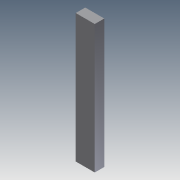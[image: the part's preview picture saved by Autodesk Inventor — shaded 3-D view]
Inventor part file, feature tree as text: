
AUTODESK INVENTOR PART (.ipt)
format: ipt  version: 2011 (Build 150239000, 239)  size: 665,088 bytes
history: native  units: in
note: dims shown in document units (in); Inventor stores cm internally (conversion verified against a paired STEP export)
features: extrude x32, sketch x32
ambient origin geometry x8: Origin, YZ Plane, XZ Plane, XY Plane, X Axis, Y Axis, Z Axis, Center Point
bodies: Solid1 (feature_tree)
feature tree (64):
  extrude  "Extrusion1"  Depth=6.75in
  extrude  "Extrusion2"  Depth=0.5in
  extrude  "Extrusion3"  Depth=0.5in
  extrude  "Extrusion4"  Depth=5.75in
  extrude  "Extrusion5"  Depth=0.5in
  extrude  "Extrusion6"  Depth=1.5in
  extrude  "Extrusion7"  Depth=1.5in
  extrude  "Extrusion8"  Depth=0.156in
  extrude  "Extrusion9"  Depth=0.25in TaperAngle=0.0deg
  extrude  "Extrusion10"  Depth=0.25in TaperAngle=0.0deg
  extrude  "Extrusion11"  Depth=0.25in TaperAngle=0.0deg
  extrude  "Extrusion12"  Depth=0.25in
  extrude  "Extrusion13"  Depth=0.25in
  extrude  "Extrusion14"  Depth=0.25in TaperAngle=0.0deg
  extrude  "Extrusion15"  Depth=3.0in
  extrude  "Extrusion16"  Depth=0.25in TaperAngle=0.0deg
  extrude  "Extrusion17"  Depth=1.0in
  extrude  "Extrusion18"  Depth=0.25in TaperAngle=0.0deg
  extrude  "Extrusion19"  Depth=0.25in TaperAngle=0.0deg
  extrude  "Extrusion20"  Depth=0.25in TaperAngle=0.0deg
  extrude  "Extrusion21"  Depth=1.0in
  extrude  "Extrusion22"  Depth=1.0in
  extrude  "Extrusion23"  Depth=2.0in
  extrude  "Extrusion24"  Depth=0.5in
  extrude  "Extrusion25"  Depth=0.5in
  extrude  "Extrusion26"  Depth=0.5in
  extrude  "Extrusion27"  Depth=0.5in
  extrude  "Extrusion28"  Depth=0.5in
  extrude  "Extrusion29"  Depth=0.5in
  extrude  "Extrusion30"  Depth=0.25in TaperAngle=0.0deg
  extrude  "Extrusion31"  Depth=1.0in
  extrude  "Extrusion32"  Depth=0.25in TaperAngle=0.0deg
  sketch  "Sketch1"  dims[d0=5.2in d1=6.75in]
  sketch  "Sketch2"  dims[d2=0.25in d3=0.5in]
  sketch  "Sketch3"  dims[d4=5.7in d5=0.5in]
  sketch  "Sketch4"  dims[d6=0.5in d7=5.75in]
  sketch  "Sketch5"  dims[d8=0.375in d9=0.5in]
  sketch  "Sketch6"  dims[d10=0.25in d11=1.5in]
  sketch  "Sketch7"  dims[d12=0.25in d13=1.5in]
  sketch  "Sketch8"  dims[d14=0.25in d15=0.156in]
  sketch  "Sketch9"  dims[d16=0.156in d17=0.25in d18=0.0in]
  sketch  "Sketch10"  dims[d19=0.125in d20=0.0in d21=0.25in d22=0.0in]
  sketch  "Sketch11"  dims[d23=0.25in d24=0.0in d25=0.25in d26=0.0in]
  sketch  "Sketch12"  dims[d27=0.25in d28=0.25in]
  sketch  "Sketch13"  dims[d29=0.25in d30=0.25in]
  sketch  "Sketch14"  dims[d31=0.25in d32=0.25in d33=0.0in]
  sketch  "Sketch15"  dims[d34=1.5in d35=3.0in]
  sketch  "Sketch16"  dims[d36=1.0in d37=0.25in d38=0.0in]
  sketch  "Sketch17"  dims[d39=6.65in d40=1.0in]
  sketch  "Sketch18"  dims[d41=1.5in d42=0.25in d43=0.0in]
  sketch  "Sketch19"  dims[d44=0.25in d45=0.0in d46=0.25in d47=0.0in]
  sketch  "Sketch20"  dims[d48=1.0in d49=0.25in d50=0.0in]
  sketch  "Sketch21"  dims[d51=0.25in d52=1.0in]
  sketch  "Sketch22"  dims[d53=0.25in d54=1.0in]
  sketch  "Sketch23"  dims[d55=0.25in d56=2.0in]
  sketch  "Sketch24"  dims[d57=1.0in d58=0.5in]
  sketch  "Sketch25"  dims[d59=1.0in d60=0.5in]
  sketch  "Sketch26"  dims[d61=1.0in d62=0.5in]
  sketch  "Sketch27"  dims[d63=1.0in d64=0.5in]
  sketch  "Sketch28"  dims[d65=1.0in d66=0.5in]
  sketch  "Sketch29"  dims[d67=1.0in d68=0.5in]
  sketch  "Sketch30"  dims[d69=1.0in d70=0.25in d71=0.0in]
  sketch  "Sketch31"  dims[d72=0.25in d73=1.0in]
  sketch  "Sketch32"  dims[d74=1.0in d75=0.25in d76=0.0in d77=0.25in d78=0.0in d79=0.25in d80=0.25in d81=0.0in d82=0.75in d83=0.156in d84=0.156in d85=0.25in d86=0.0in d87=0.25in d88=0.0in d89=1.0in d90=1.0in d91=1.0in d92=0.25in d93=0.0in d94=1.0in d95=0.0in d96=1.0in d97=0.0in d98=1.0in d99=0.0in d100=0.5in d101=0.0in d102=0.5in d103=0.0in d104=0.25in d105=0.5in d106=0.0in d107=0.5in d108=0.0in d109=0.25in d110=0.0in d111=0.25in d112=0.0in d113=0.25in d114=0.5in d115=0.0in d116=0.25in d117=0.0in d118=0.5in d119=0.0in d120=0.25in d121=0.0in d122=0.75in d123=0.0in]
